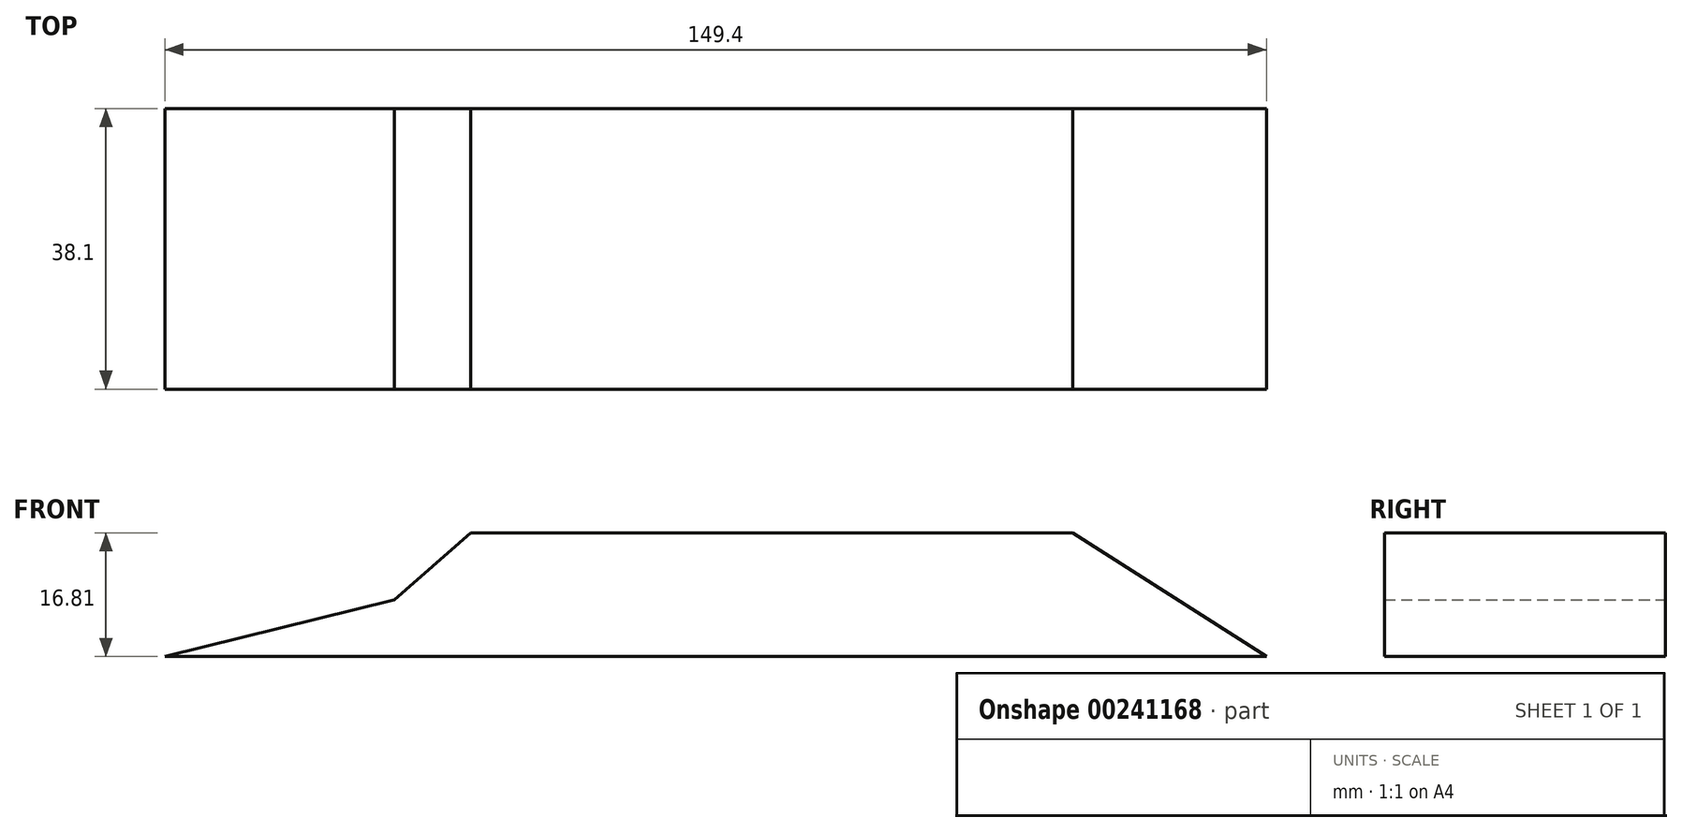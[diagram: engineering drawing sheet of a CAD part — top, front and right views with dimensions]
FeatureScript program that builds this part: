
annotation { "Feature Type Name" : "Feature", "Feature Type Description" : "" }
export const myFeature = defineFeature(function(context is Context, id is Id, definition is map)
    precondition{}
    {
        {
            var Q0;
            Q0=qCreatedBy(makeId("Front.planeOp"),FACE);
            var sketch = newSketch(context, id + "F0", { "sketchPlane" : qUnion([Q0])});
            skLineSegment(sketch, "E0", {"start": v(-76.1, 0) * mm, "end": v(-45, 7.71) * mm});
            skLineSegment(sketch, "E1", {"start": v(-45, 7.71) * mm, "end": v(-34.63, 16.81) * mm});
            skLineSegment(sketch, "E2", {"start": v(-34.63, 16.81) * mm, "end": v(47.02, 16.81) * mm});
            skLineSegment(sketch, "E3", {"start": v(47.02, 16.81) * mm, "end": v(73.31, 0) * mm});
            skLineSegment(sketch, "E4", {"start": v(73.31, 0) * mm, "end": v(-76.1, 0) * mm});
            skSolve(sketch);
        }
        {
            var Q0;
            Q0=makeQuery(id+"F0.imprint","IMPRINT",FACE,{"disambiguationData":[TD([[makeQuery(id+"F0.imprint","IMPRINT",EDGE,{"derivedFrom":sQuery(id+"F0.wireOp",EDGE,"E0")}),-1.0]])]});
            extrude(context, id + "F1", {"entities" : qUnion([Q0]), "depth" : 38.1 * mm});
        }
    });
